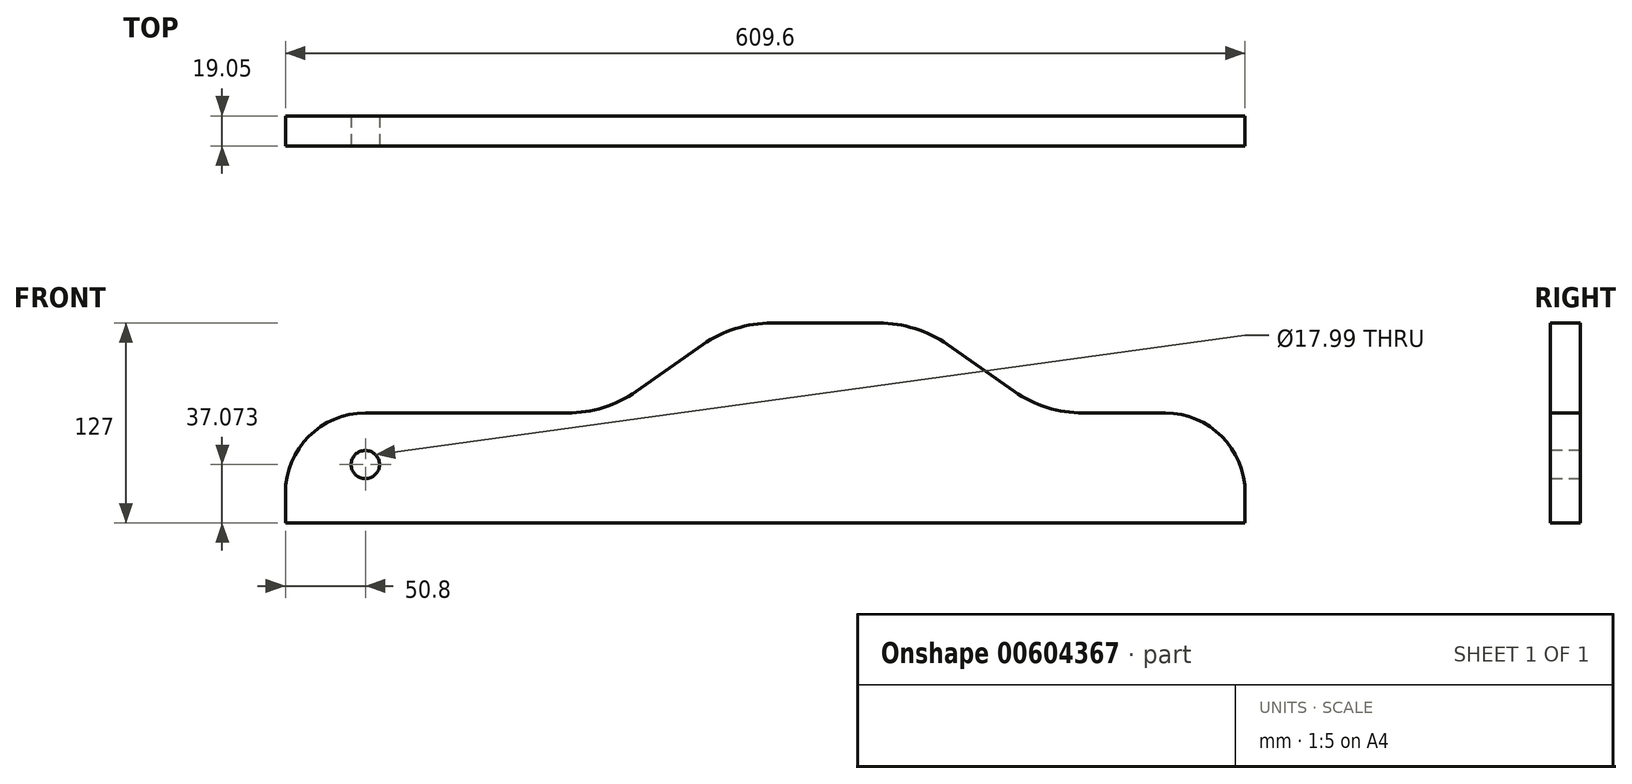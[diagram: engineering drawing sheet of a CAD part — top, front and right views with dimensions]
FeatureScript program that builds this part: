
annotation { "Feature Type Name" : "Feature", "Feature Type Description" : "" }
export const myFeature = defineFeature(function(context is Context, id is Id, definition is map)
    precondition{}
    {
        {
            var Q0;
            Q0=qCreatedBy(makeId("Front.planeOp"),FACE);
            var sketch = newSketch(context, id + "F0", { "sketchPlane" : qUnion([Q0])});
            skLineSegment(sketch, "E0", {"start": v(-342.9, 0) * mm, "end": v(-342.9, 69.85) * mm});
            skLineSegment(sketch, "E1", {"start": v(-342.9, 69.85) * mm, "end": v(-139.7, 69.85) * mm});
            skLineSegment(sketch, "E2", {"start": v(-139.7, 69.85) * mm, "end": v(-58.08, 127) * mm});
            skLineSegment(sketch, "E3", {"start": v(-58.08, 127) * mm, "end": v(58.08, 127) * mm});
            skLineSegment(sketch, "E4", {"start": v(58.08, 127) * mm, "end": v(139.7, 69.85) * mm});
            skLineSegment(sketch, "E5", {"start": v(139.7, 69.85) * mm, "end": v(266.7, 69.85) * mm});
            skLineSegment(sketch, "E6", {"start": v(266.7, 69.85) * mm, "end": v(266.7, 0) * mm});
            skLineSegment(sketch, "E7", {"start": v(266.7, 0) * mm, "end": v(-342.9, 0) * mm});
            skSolve(sketch);
        }
        {
            var Q0;
            Q0=makeQuery(id+"F0.imprint","IMPRINT",FACE,{"disambiguationData":[TD([[makeQuery(id+"F0.imprint","IMPRINT",EDGE,{"derivedFrom":sQuery(id+"F0.wireOp",EDGE,"E0")}),-1.0]])]});
            extrude(context, id + "F1", {"entities" : qUnion([Q0]), "depth" : 19.05 * mm, "offsetDistance" : 25.4 * mm});
        }
        {
            var Q0;
            Q0=makeQuery(id+"F1.opExtrude","SWEPT_EDGE",EDGE,{"disambiguationData":[OSD([sQuery(id+"F0.wireOp",EDGE,"E4"),sQuery(id+"F0.wireOp",EDGE,"E5")])]});
            var Q1;
            Q1=makeQuery(id+"F1.opExtrude","SWEPT_EDGE",EDGE,{"disambiguationData":[OSD([sQuery(id+"F0.wireOp",EDGE,"E3"),sQuery(id+"F0.wireOp",EDGE,"E4")])]});
            var Q2;
            Q2=makeQuery(id+"F1.opExtrude","SWEPT_EDGE",EDGE,{"disambiguationData":[OSD([sQuery(id+"F0.wireOp",EDGE,"E2"),sQuery(id+"F0.wireOp",EDGE,"E3")])]});
            var Q3;
            Q3=makeQuery(id+"F1.opExtrude","SWEPT_EDGE",EDGE,{"disambiguationData":[OSD([sQuery(id+"F0.wireOp",EDGE,"E1"),sQuery(id+"F0.wireOp",EDGE,"E2")])]});
            fillet(context, id + "F2", {"entities" : qUnion([Q0, Q1, Q2, Q3]), "radius" : 76.2 * mm, "tangentPropagation" : true, "allowEdgeOverflow" : false});
        }
        {
            var Q0;
            Q0=makeQuery(id+"F1.opExtrude","SWEPT_EDGE",EDGE,{"disambiguationData":[OSD([sQuery(id+"F0.wireOp",EDGE,"E5"),sQuery(id+"F0.wireOp",EDGE,"E6")])]});
            var Q1;
            Q1=makeQuery(id+"F1.opExtrude","SWEPT_EDGE",EDGE,{"disambiguationData":[OSD([sQuery(id+"F0.wireOp",EDGE,"E0"),sQuery(id+"F0.wireOp",EDGE,"E1")])]});
            fillet(context, id + "F3", {"entities" : qUnion([Q0, Q1]), "radius" : 50.8 * mm, "tangentPropagation" : true, "allowEdgeOverflow" : false});
        }
        {
            var Q0;
            Q0=makeQuery(id+"F1.opExtrude","CAP_FACE",FACE,{"disambiguationData":[OSD([sQuery(id+"F0.wireOp",EDGE,"E0"),sQuery(id+"F0.wireOp",EDGE,"E1"),sQuery(id+"F0.wireOp",EDGE,"E2"),sQuery(id+"F0.wireOp",EDGE,"E3"),sQuery(id+"F0.wireOp",EDGE,"E4"),sQuery(id+"F0.wireOp",EDGE,"E5"),sQuery(id+"F0.wireOp",EDGE,"E6"),sQuery(id+"F0.wireOp",EDGE,"E7")])],"isStart":false});
            var sketch = newSketch(context, id + "F4", { "sketchPlane" : qUnion([Q0])});
            skCircle(sketch, "E8", {"center": v(-292.1, 37.07) * mm, "radius": 9 * mm});
            skSolve(sketch);
        }
        {
            var Q0;
            Q0=makeQuery(id+"F4.imprint","IMPRINT",FACE,{"disambiguationData":[TD([[makeQuery(id+"F4.imprint","IMPRINT",EDGE,{"derivedFrom":sQuery(id+"F4.wireOp",EDGE,"E8")}),1.0]])]});
            extrude(context, id + "F5", {"entities" : qUnion([Q0]), "operationType" : NewBodyOperationType.REMOVE, "oppositeDirection" : true, "depth" : 25.4 * mm, "offsetDistance" : 25.4 * mm});
        }
    });
